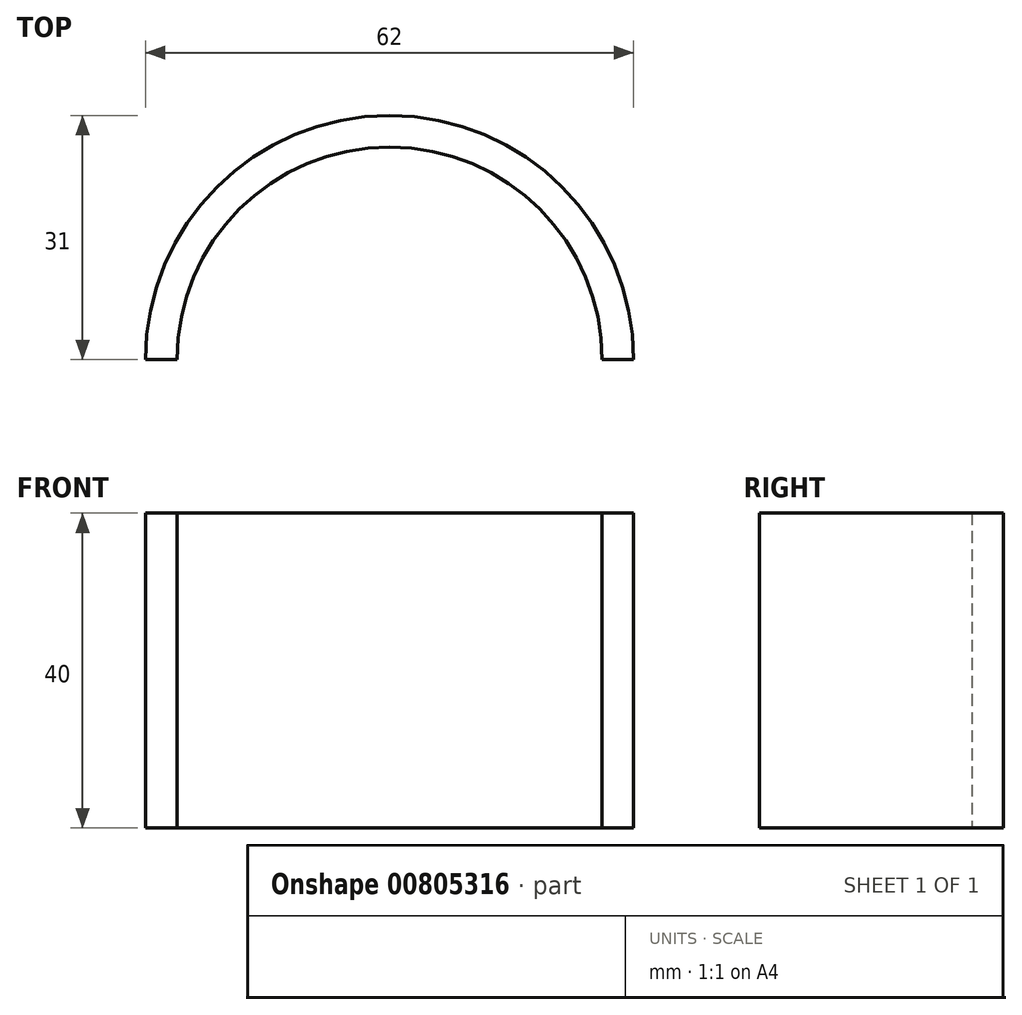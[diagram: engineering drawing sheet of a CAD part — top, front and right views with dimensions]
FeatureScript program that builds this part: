
annotation { "Feature Type Name" : "Feature", "Feature Type Description" : "" }
export const myFeature = defineFeature(function(context is Context, id is Id, definition is map)
    precondition{}
    {
        {
            var Q0;
            Q0=qCreatedBy(makeId("Top.planeOp"),FACE);
            var sketch = newSketch(context, id + "F0", { "sketchPlane" : qUnion([Q0])});
            skArc(sketch, "E0", {"start": v(27, 0) * mm, "mid": v(0, 27) * mm, "end": v(-27, 0) * mm});
            skArc(sketch, "E1.0", {"start": v(31, 0) * mm, "mid": v(0, 31) * mm, "end": v(-31, 0) * mm});
            skLineSegment(sketch, "E2", {"start": v(-31, 0) * mm, "end": v(-27, 0) * mm});
            skLineSegment(sketch, "E3", {"start": v(27, 0) * mm, "end": v(31, 0) * mm});
            skSolve(sketch);
        }
        {
            var Q0;
            Q0=makeQuery(id+"F0.imprint","IMPRINT",FACE,{"disambiguationData":[TD([[makeQuery(id+"F0.imprint","IMPRINT",EDGE,{"derivedFrom":sQuery(id+"F0.wireOp",EDGE,"E0")}),-1.0]])]});
            extrude(context, id + "F1", {"entities" : qUnion([Q0]), "depth" : 40 * mm, "offsetDistance" : 25 * mm});
        }
    });
